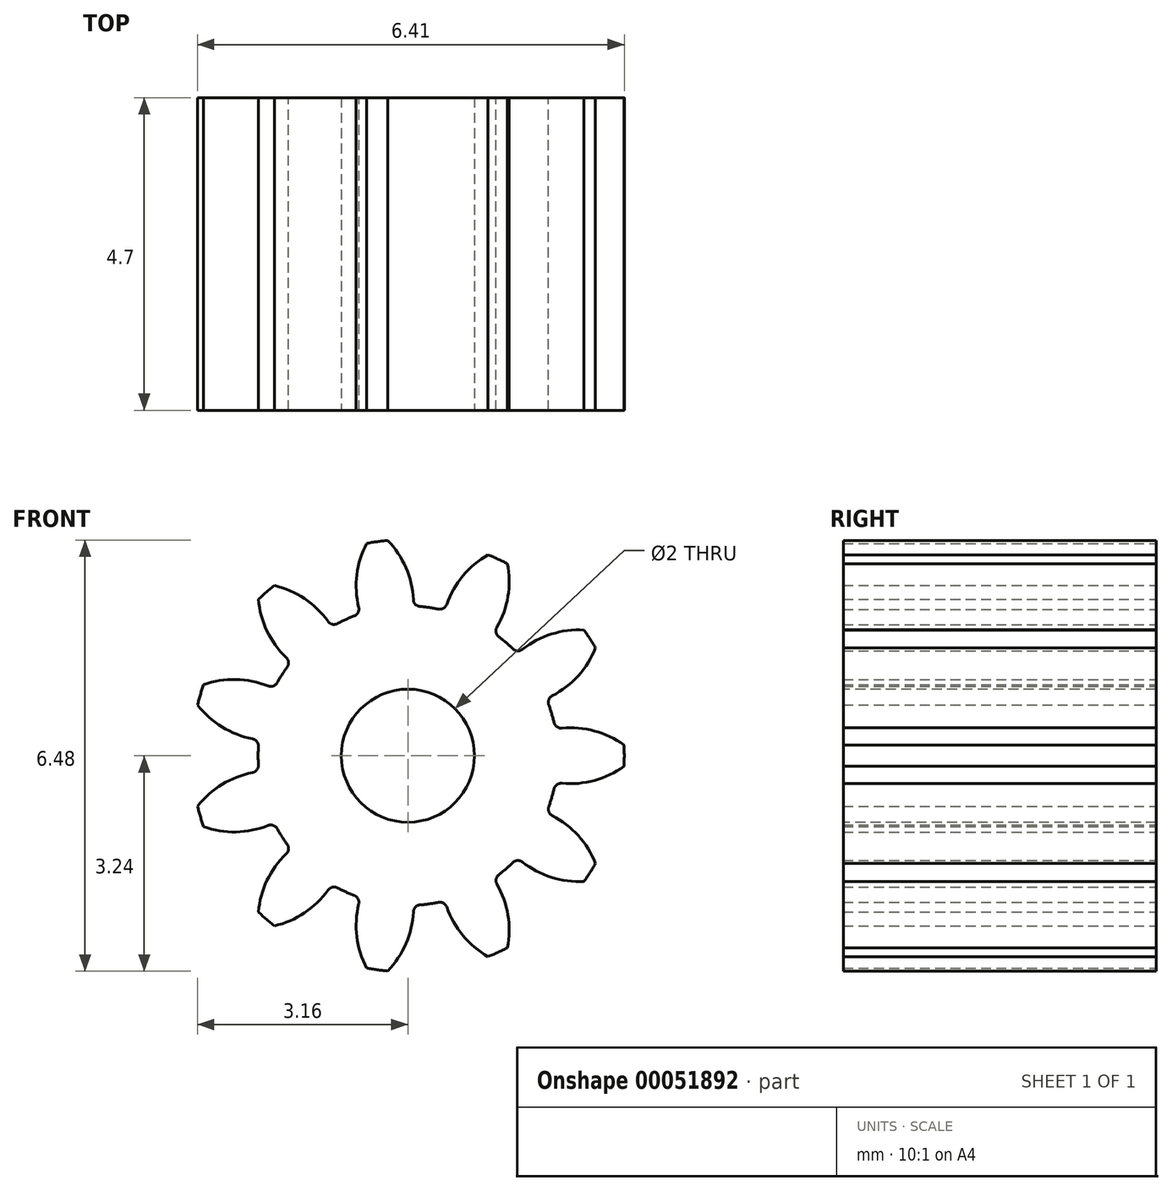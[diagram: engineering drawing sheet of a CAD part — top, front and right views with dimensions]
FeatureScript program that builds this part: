
annotation { "Feature Type Name" : "Feature", "Feature Type Description" : "" }
export const myFeature = defineFeature(function(context is Context, id is Id, definition is map)
    precondition{}
    {
        {
            var Q0;
            Q0=qCreatedBy(makeId("Front.planeOp"),FACE);
            var sketch = newSketch(context, id + "F0", { "sketchPlane" : qUnion([Q0])});
            skCircle(sketch, "E0", {"center": v(0, 0) * mm, "radius": 3.25 * mm, "construction": true});
            skCircle(sketch, "E1", {"center": v(0, 0) * mm, "radius": 2.25 * mm, "construction": true});
            skCircle(sketch, "E2", {"center": v(0, 0) * mm, "radius": 2.75 * mm, "construction": true});
            skLineSegment(sketch, "E3", {"start": v(0, 0) * mm, "end": v(0, 5.25) * mm, "construction": true});
            skLineSegment(sketch, "E4", {"start": v(0, 2.75) * mm, "end": v(-5.58, 2.75) * mm, "construction": true});
            skLineSegment(sketch, "E5", {"start": v(0, 2.75) * mm, "end": v(-4.16, 1.24) * mm, "construction": true});
            skCircle(sketch, "E6", {"center": v(0, 2.75) * mm, "radius": 1.38 * mm, "construction": true});
            skCircle(sketch, "E7.cCircle", {"center": v(0, 0) * mm, "radius": 5.25 * mm, "construction": true});
            skLineSegment(sketch, "E7.0", {"start": v(0, 5.25) * mm, "end": v(0.75, 5.2) * mm, "construction": true});
            skLineSegment(sketch, "E7.1", {"start": v(0.75, 5.2) * mm, "end": v(1.48, 5.04) * mm, "construction": true});
            skLineSegment(sketch, "E7.2", {"start": v(1.48, 5.04) * mm, "end": v(2.18, 4.78) * mm, "construction": true});
            skLineSegment(sketch, "E7.3", {"start": v(2.18, 4.78) * mm, "end": v(2.84, 4.42) * mm, "construction": true});
            skLineSegment(sketch, "E7.4", {"start": v(2.84, 4.42) * mm, "end": v(3.44, 3.97) * mm, "construction": true});
            skLineSegment(sketch, "E7.5", {"start": v(3.44, 3.97) * mm, "end": v(3.97, 3.44) * mm, "construction": true});
            skLineSegment(sketch, "E7.6", {"start": v(3.97, 3.44) * mm, "end": v(4.42, 2.84) * mm, "construction": true});
            skLineSegment(sketch, "E7.7", {"start": v(4.42, 2.84) * mm, "end": v(4.78, 2.18) * mm, "construction": true});
            skLineSegment(sketch, "E7.8", {"start": v(4.78, 2.18) * mm, "end": v(5.04, 1.48) * mm, "construction": true});
            skLineSegment(sketch, "E7.9", {"start": v(5.04, 1.48) * mm, "end": v(5.2, 0.75) * mm, "construction": true});
            skLineSegment(sketch, "E7.10", {"start": v(5.2, 0.75) * mm, "end": v(5.25, 0) * mm, "construction": true});
            skLineSegment(sketch, "E7.11", {"start": v(5.25, 0) * mm, "end": v(5.2, -0.75) * mm, "construction": true});
            skLineSegment(sketch, "E7.12", {"start": v(5.2, -0.75) * mm, "end": v(5.04, -1.48) * mm, "construction": true});
            skLineSegment(sketch, "E7.13", {"start": v(5.04, -1.48) * mm, "end": v(4.78, -2.18) * mm, "construction": true});
            skLineSegment(sketch, "E7.14", {"start": v(4.78, -2.18) * mm, "end": v(4.42, -2.84) * mm, "construction": true});
            skLineSegment(sketch, "E7.15", {"start": v(4.42, -2.84) * mm, "end": v(3.97, -3.44) * mm, "construction": true});
            skLineSegment(sketch, "E7.16", {"start": v(3.97, -3.44) * mm, "end": v(3.44, -3.97) * mm, "construction": true});
            skLineSegment(sketch, "E7.17", {"start": v(3.44, -3.97) * mm, "end": v(2.84, -4.42) * mm, "construction": true});
            skLineSegment(sketch, "E7.18", {"start": v(2.84, -4.42) * mm, "end": v(2.18, -4.78) * mm, "construction": true});
            skLineSegment(sketch, "E7.19", {"start": v(2.18, -4.78) * mm, "end": v(1.48, -5.04) * mm, "construction": true});
            skLineSegment(sketch, "E7.20", {"start": v(1.48, -5.04) * mm, "end": v(0.75, -5.2) * mm, "construction": true});
            skLineSegment(sketch, "E7.21", {"start": v(0.75, -5.2) * mm, "end": v(0, -5.25) * mm, "construction": true});
            skLineSegment(sketch, "E7.22", {"start": v(0, -5.25) * mm, "end": v(-0.75, -5.2) * mm, "construction": true});
            skLineSegment(sketch, "E7.23", {"start": v(-0.75, -5.2) * mm, "end": v(-1.48, -5.04) * mm, "construction": true});
            skLineSegment(sketch, "E7.24", {"start": v(-1.48, -5.04) * mm, "end": v(-2.18, -4.78) * mm, "construction": true});
            skLineSegment(sketch, "E7.25", {"start": v(-2.18, -4.78) * mm, "end": v(-2.84, -4.42) * mm, "construction": true});
            skLineSegment(sketch, "E7.26", {"start": v(-2.84, -4.42) * mm, "end": v(-3.44, -3.97) * mm, "construction": true});
            skLineSegment(sketch, "E7.27", {"start": v(-3.44, -3.97) * mm, "end": v(-3.97, -3.44) * mm, "construction": true});
            skLineSegment(sketch, "E7.28", {"start": v(-3.97, -3.44) * mm, "end": v(-4.42, -2.84) * mm, "construction": true});
            skLineSegment(sketch, "E7.29", {"start": v(-4.42, -2.84) * mm, "end": v(-4.78, -2.18) * mm, "construction": true});
            skLineSegment(sketch, "E7.30", {"start": v(-4.78, -2.18) * mm, "end": v(-5.04, -1.48) * mm, "construction": true});
            skLineSegment(sketch, "E7.31", {"start": v(-5.04, -1.48) * mm, "end": v(-5.2, -0.75) * mm, "construction": true});
            skLineSegment(sketch, "E7.32", {"start": v(-5.2, -0.75) * mm, "end": v(-5.25, 0) * mm, "construction": true});
            skLineSegment(sketch, "E7.33", {"start": v(-5.25, 0) * mm, "end": v(-5.2, 0.75) * mm, "construction": true});
            skLineSegment(sketch, "E7.34", {"start": v(-5.2, 0.75) * mm, "end": v(-5.04, 1.48) * mm, "construction": true});
            skLineSegment(sketch, "E7.35", {"start": v(-5.04, 1.48) * mm, "end": v(-4.78, 2.18) * mm, "construction": true});
            skLineSegment(sketch, "E7.36", {"start": v(-4.78, 2.18) * mm, "end": v(-4.42, 2.84) * mm, "construction": true});
            skLineSegment(sketch, "E7.37", {"start": v(-4.42, 2.84) * mm, "end": v(-3.97, 3.44) * mm, "construction": true});
            skLineSegment(sketch, "E7.38", {"start": v(-3.97, 3.44) * mm, "end": v(-3.44, 3.97) * mm, "construction": true});
            skLineSegment(sketch, "E7.39", {"start": v(-3.44, 3.97) * mm, "end": v(-2.84, 4.42) * mm, "construction": true});
            skLineSegment(sketch, "E7.40", {"start": v(-2.84, 4.42) * mm, "end": v(-2.18, 4.78) * mm, "construction": true});
            skLineSegment(sketch, "E7.41", {"start": v(-2.18, 4.78) * mm, "end": v(-1.48, 5.04) * mm, "construction": true});
            skLineSegment(sketch, "E7.42", {"start": v(-1.48, 5.04) * mm, "end": v(-0.75, 5.2) * mm, "construction": true});
            skLineSegment(sketch, "E7.43", {"start": v(-0.75, 5.2) * mm, "end": v(0, 5.25) * mm, "construction": true});
            skLineSegment(sketch, "E8", {"start": v(-1.48, 5.04) * mm, "end": v(0, 0) * mm, "construction": true});
            skLineSegment(sketch, "E9", {"start": v(-0.75, 5.2) * mm, "end": v(0, 0) * mm, "construction": true});
            skArc(sketch, "E10", {"start": v(0.08, 2.35) * mm, "mid": v(-2.67, 2.26) * mm, "end": v(0.08, 2.25) * mm, "construction": true});
            skArc(sketch, "E11", {"start": v(-0.3, 3.24) * mm, "mid": v(-0.03, 2.83) * mm, "end": v(0.08, 2.35) * mm});
            skArc(sketch, "E12.MirrorCS", {"start": v(-0.62, 3.2) * mm, "mid": v(-0.77, 2.72) * mm, "end": v(-0.74, 2.23) * mm});
            skArc(sketch, "E13", {"start": v(-0.62, 3.2) * mm, "mid": v(-0.46, 3.22) * mm, "end": v(-0.3, 3.24) * mm});
            skArc(sketch, "E14", {"start": v(-0.8, 2.1) * mm, "mid": v(0.32, -2.23) * mm, "end": v(0.18, 2.24) * mm});
            skArc(sketch, "E15.1.0", {"start": v(-2.25, 2.35) * mm, "mid": v(-2.1, 1.83) * mm, "end": v(-1.75, 1.41) * mm});
            skArc(sketch, "E15.1.1", {"start": v(-2.25, 2.35) * mm, "mid": v(-2.13, 2.46) * mm, "end": v(-2, 2.56) * mm});
            skArc(sketch, "E15.1.2", {"start": v(-2, 2.56) * mm, "mid": v(-1.51, 2.33) * mm, "end": v(-1.15, 1.94) * mm});
            skArc(sketch, "E15.2.0", {"start": v(-3.16, 0.76) * mm, "mid": v(-2.75, 0.4) * mm, "end": v(-2.24, 0.24) * mm});
            skArc(sketch, "E15.2.1", {"start": v(-3.16, 0.76) * mm, "mid": v(-3.12, 0.92) * mm, "end": v(-3.07, 1.07) * mm});
            skArc(sketch, "E15.2.2", {"start": v(-3.07, 1.07) * mm, "mid": v(-2.53, 1.14) * mm, "end": v(-2.01, 1) * mm});
            skArc(sketch, "E15.3.0", {"start": v(-3.07, -1.07) * mm, "mid": v(-2.53, -1.14) * mm, "end": v(-2.01, -1) * mm});
            skArc(sketch, "E15.3.1", {"start": v(-3.07, -1.07) * mm, "mid": v(-3.12, -0.92) * mm, "end": v(-3.16, -0.76) * mm});
            skArc(sketch, "E15.3.2", {"start": v(-3.16, -0.76) * mm, "mid": v(-2.75, -0.4) * mm, "end": v(-2.24, -0.24) * mm});
            skArc(sketch, "E15.4.0", {"start": v(-2, -2.56) * mm, "mid": v(-1.51, -2.33) * mm, "end": v(-1.15, -1.94) * mm});
            skArc(sketch, "E15.4.1", {"start": v(-2, -2.56) * mm, "mid": v(-2.13, -2.46) * mm, "end": v(-2.25, -2.35) * mm});
            skArc(sketch, "E15.4.2", {"start": v(-2.25, -2.35) * mm, "mid": v(-2.1, -1.83) * mm, "end": v(-1.75, -1.41) * mm});
            skArc(sketch, "E15.5.0", {"start": v(-0.3, -3.24) * mm, "mid": v(-0.01, -2.78) * mm, "end": v(0.08, -2.25) * mm});
            skArc(sketch, "E15.5.1", {"start": v(-0.3, -3.24) * mm, "mid": v(-0.46, -3.22) * mm, "end": v(-0.62, -3.2) * mm});
            skArc(sketch, "E15.5.2", {"start": v(-0.62, -3.2) * mm, "mid": v(-0.77, -2.67) * mm, "end": v(-0.71, -2.13) * mm});
            skArc(sketch, "E15.6.0", {"start": v(1.5, -2.89) * mm, "mid": v(1.5, -2.35) * mm, "end": v(1.29, -1.85) * mm});
            skArc(sketch, "E15.6.1", {"start": v(1.5, -2.89) * mm, "mid": v(1.35, -2.96) * mm, "end": v(1.2, -3.02) * mm});
            skArc(sketch, "E15.6.2", {"start": v(1.2, -3.02) * mm, "mid": v(0.8, -2.66) * mm, "end": v(0.55, -2.18) * mm});
            skArc(sketch, "E15.7.0", {"start": v(2.82, -1.62) * mm, "mid": v(2.52, -1.17) * mm, "end": v(2.08, -0.86) * mm});
            skArc(sketch, "E15.7.1", {"start": v(2.82, -1.62) * mm, "mid": v(2.73, -1.76) * mm, "end": v(2.64, -1.89) * mm});
            skArc(sketch, "E15.7.2", {"start": v(2.64, -1.89) * mm, "mid": v(2.1, -1.81) * mm, "end": v(1.65, -1.53) * mm});
            skArc(sketch, "E15.8.0", {"start": v(3.25, 0.16) * mm, "mid": v(2.75, 0.38) * mm, "end": v(2.21, 0.4) * mm});
            skArc(sketch, "E15.8.1", {"start": v(3.25, 0.16) * mm, "mid": v(3.25, 0) * mm, "end": v(3.25, -0.16) * mm});
            skArc(sketch, "E15.8.2", {"start": v(3.25, -0.16) * mm, "mid": v(2.75, -0.38) * mm, "end": v(2.21, -0.4) * mm});
            skArc(sketch, "E15.9.0", {"start": v(2.64, 1.89) * mm, "mid": v(2.1, 1.81) * mm, "end": v(1.65, 1.53) * mm});
            skArc(sketch, "E15.9.1", {"start": v(2.64, 1.89) * mm, "mid": v(2.73, 1.76) * mm, "end": v(2.82, 1.62) * mm});
            skArc(sketch, "E15.9.2", {"start": v(2.82, 1.62) * mm, "mid": v(2.52, 1.17) * mm, "end": v(2.08, 0.86) * mm});
            skArc(sketch, "E15.10.0", {"start": v(1.2, 3.02) * mm, "mid": v(0.8, 2.66) * mm, "end": v(0.55, 2.18) * mm});
            skArc(sketch, "E15.10.1", {"start": v(1.2, 3.02) * mm, "mid": v(1.35, 2.96) * mm, "end": v(1.5, 2.89) * mm});
            skArc(sketch, "E15.10.2", {"start": v(1.5, 2.89) * mm, "mid": v(1.5, 2.35) * mm, "end": v(1.29, 1.85) * mm});
            skPoint(sketch, "E16.visualSharp", {"position": v(0.08, 2.25) * mm});
            skArc(sketch, "E16.filletArc", {"start": v(0.08, 2.35) * mm, "mid": v(0.11, 2.28) * mm, "end": v(0.18, 2.24) * mm});
            skPoint(sketch, "E17.visualSharp", {"position": v(-0.71, 2.13) * mm});
            skArc(sketch, "E17.filletArc", {"start": v(-0.8, 2.1) * mm, "mid": v(-0.75, 2.15) * mm, "end": v(-0.74, 2.23) * mm});
            skArc(sketch, "E18.1.0", {"start": v(-2, 2.56) * mm, "mid": v(-1.55, 2.36) * mm, "end": v(-1.2, 2.02) * mm});
            skArc(sketch, "E18.1.2", {"start": v(-2.25, 2.35) * mm, "mid": v(-2.12, 1.87) * mm, "end": v(-1.83, 1.48) * mm});
            skArc(sketch, "E18.1.3", {"start": v(-1.81, 1.33) * mm, "mid": v(-1.8, 1.4) * mm, "end": v(-1.83, 1.48) * mm});
            skArc(sketch, "E18.1.4", {"start": v(-1.2, 2.02) * mm, "mid": v(-1.14, 1.98) * mm, "end": v(-1.06, 1.99) * mm});
            skArc(sketch, "E18.2.0", {"start": v(-3.07, 1.07) * mm, "mid": v(-2.58, 1.15) * mm, "end": v(-2.1, 1.05) * mm});
            skArc(sketch, "E18.2.2", {"start": v(-3.16, 0.76) * mm, "mid": v(-2.8, 0.43) * mm, "end": v(-2.33, 0.25) * mm});
            skArc(sketch, "E18.2.3", {"start": v(-2.25, 0.14) * mm, "mid": v(-2.27, 0.21) * mm, "end": v(-2.33, 0.25) * mm});
            skArc(sketch, "E18.2.4", {"start": v(-2.1, 1.05) * mm, "mid": v(-2.02, 1.05) * mm, "end": v(-1.96, 1.1) * mm});
            skArc(sketch, "E18.3.0", {"start": v(-3.16, -0.76) * mm, "mid": v(-2.8, -0.43) * mm, "end": v(-2.33, -0.25) * mm});
            skArc(sketch, "E18.3.2", {"start": v(-3.07, -1.07) * mm, "mid": v(-2.58, -1.15) * mm, "end": v(-2.1, -1.05) * mm});
            skArc(sketch, "E18.3.3", {"start": v(-1.96, -1.1) * mm, "mid": v(-2.02, -1.05) * mm, "end": v(-2.1, -1.05) * mm});
            skArc(sketch, "E18.3.4", {"start": v(-2.33, -0.25) * mm, "mid": v(-2.27, -0.21) * mm, "end": v(-2.25, -0.14) * mm});
            skArc(sketch, "E18.4.0", {"start": v(-2.25, -2.35) * mm, "mid": v(-2.12, -1.87) * mm, "end": v(-1.83, -1.48) * mm});
            skArc(sketch, "E18.4.2", {"start": v(-2, -2.56) * mm, "mid": v(-1.55, -2.36) * mm, "end": v(-1.2, -2.02) * mm});
            skArc(sketch, "E18.4.3", {"start": v(-1.06, -1.99) * mm, "mid": v(-1.14, -1.98) * mm, "end": v(-1.2, -2.02) * mm});
            skArc(sketch, "E18.4.4", {"start": v(-1.83, -1.48) * mm, "mid": v(-1.8, -1.4) * mm, "end": v(-1.81, -1.33) * mm});
            skArc(sketch, "E18.5.0", {"start": v(-0.62, -3.2) * mm, "mid": v(-0.77, -2.72) * mm, "end": v(-0.74, -2.23) * mm});
            skArc(sketch, "E18.5.2", {"start": v(-0.3, -3.24) * mm, "mid": v(-0.03, -2.83) * mm, "end": v(0.08, -2.35) * mm});
            skArc(sketch, "E18.5.3", {"start": v(0.18, -2.24) * mm, "mid": v(0.11, -2.28) * mm, "end": v(0.08, -2.35) * mm});
            skArc(sketch, "E18.5.4", {"start": v(-0.74, -2.23) * mm, "mid": v(-0.75, -2.15) * mm, "end": v(-0.8, -2.1) * mm});
            skArc(sketch, "E18.6.0", {"start": v(1.2, -3.02) * mm, "mid": v(0.83, -2.7) * mm, "end": v(0.58, -2.27) * mm});
            skArc(sketch, "E18.6.2", {"start": v(1.5, -2.89) * mm, "mid": v(1.5, -2.4) * mm, "end": v(1.34, -1.93) * mm});
            skArc(sketch, "E18.6.3", {"start": v(1.37, -1.79) * mm, "mid": v(1.32, -1.85) * mm, "end": v(1.34, -1.93) * mm});
            skArc(sketch, "E18.6.4", {"start": v(0.58, -2.27) * mm, "mid": v(0.53, -2.22) * mm, "end": v(0.46, -2.2) * mm});
            skArc(sketch, "E18.7.0", {"start": v(2.64, -1.89) * mm, "mid": v(2.16, -1.83) * mm, "end": v(1.72, -1.6) * mm});
            skArc(sketch, "E18.7.2", {"start": v(2.82, -1.62) * mm, "mid": v(2.56, -1.2) * mm, "end": v(2.17, -0.9) * mm});
            skArc(sketch, "E18.7.3", {"start": v(2.12, -0.77) * mm, "mid": v(2.12, -0.84) * mm, "end": v(2.17, -0.9) * mm});
            skArc(sketch, "E18.7.4", {"start": v(1.72, -1.6) * mm, "mid": v(1.65, -1.58) * mm, "end": v(1.58, -1.6) * mm});
            skArc(sketch, "E18.8.0", {"start": v(3.25, -0.16) * mm, "mid": v(2.8, -0.37) * mm, "end": v(2.31, -0.41) * mm});
            skArc(sketch, "E18.8.2", {"start": v(3.25, 0.16) * mm, "mid": v(2.8, 0.37) * mm, "end": v(2.31, 0.41) * mm});
            skArc(sketch, "E18.8.3", {"start": v(2.2, 0.5) * mm, "mid": v(2.24, 0.43) * mm, "end": v(2.31, 0.41) * mm});
            skArc(sketch, "E18.8.4", {"start": v(2.31, -0.41) * mm, "mid": v(2.24, -0.43) * mm, "end": v(2.2, -0.5) * mm});
            skArc(sketch, "E18.9.0", {"start": v(2.82, 1.62) * mm, "mid": v(2.56, 1.2) * mm, "end": v(2.17, 0.9) * mm});
            skArc(sketch, "E18.9.2", {"start": v(2.64, 1.89) * mm, "mid": v(2.16, 1.83) * mm, "end": v(1.72, 1.6) * mm});
            skArc(sketch, "E18.9.3", {"start": v(1.58, 1.6) * mm, "mid": v(1.65, 1.58) * mm, "end": v(1.72, 1.6) * mm});
            skArc(sketch, "E18.9.4", {"start": v(2.17, 0.9) * mm, "mid": v(2.12, 0.84) * mm, "end": v(2.12, 0.77) * mm});
            skArc(sketch, "E18.10.0", {"start": v(1.5, 2.89) * mm, "mid": v(1.5, 2.4) * mm, "end": v(1.34, 1.93) * mm});
            skArc(sketch, "E18.10.2", {"start": v(1.2, 3.02) * mm, "mid": v(0.83, 2.7) * mm, "end": v(0.58, 2.27) * mm});
            skArc(sketch, "E18.10.3", {"start": v(0.46, 2.2) * mm, "mid": v(0.53, 2.22) * mm, "end": v(0.58, 2.27) * mm});
            skArc(sketch, "E18.10.4", {"start": v(1.34, 1.93) * mm, "mid": v(1.32, 1.85) * mm, "end": v(1.37, 1.79) * mm});
            skSolve(sketch);
        }
        {
            var Q0;
            Q0 = qSketchRegion(id + "F0", true);
            extrude(context, id + "F1", {"entities" : qUnion([Q0]), "depth" : 4.7 * mm});
        }
        {
            var Q0;
            Q0=makeQuery(id+"F1.opExtrude","CAP_FACE",FACE,{"disambiguationData":[OSD([sQuery(id+"F0.wireOp",EDGE,"E11"),sQuery(id+"F0.wireOp",EDGE,"E12.MirrorCS"),sQuery(id+"F0.wireOp",EDGE,"E13"),sQuery(id+"F0.wireOp",EDGE,"E14"),sQuery(id+"F0.wireOp",EDGE,"E15.1.0"),sQuery(id+"F0.wireOp",EDGE,"E15.1.1"),sQuery(id+"F0.wireOp",EDGE,"E15.1.2"),sQuery(id+"F0.wireOp",EDGE,"E15.2.0"),sQuery(id+"F0.wireOp",EDGE,"E15.2.1"),sQuery(id+"F0.wireOp",EDGE,"E15.2.2"),sQuery(id+"F0.wireOp",EDGE,"E15.3.0"),sQuery(id+"F0.wireOp",EDGE,"E15.3.1"),sQuery(id+"F0.wireOp",EDGE,"E15.3.2"),sQuery(id+"F0.wireOp",EDGE,"E15.4.0"),sQuery(id+"F0.wireOp",EDGE,"E15.4.1"),sQuery(id+"F0.wireOp",EDGE,"E15.4.2"),sQuery(id+"F0.wireOp",EDGE,"E15.5.0"),sQuery(id+"F0.wireOp",EDGE,"E15.5.1"),sQuery(id+"F0.wireOp",EDGE,"E15.5.2"),sQuery(id+"F0.wireOp",EDGE,"E15.6.0"),sQuery(id+"F0.wireOp",EDGE,"E15.6.1"),sQuery(id+"F0.wireOp",EDGE,"E15.6.2"),sQuery(id+"F0.wireOp",EDGE,"E15.7.0"),sQuery(id+"F0.wireOp",EDGE,"E15.7.1"),sQuery(id+"F0.wireOp",EDGE,"E15.7.2"),sQuery(id+"F0.wireOp",EDGE,"E15.8.0"),sQuery(id+"F0.wireOp",EDGE,"E15.8.1"),sQuery(id+"F0.wireOp",EDGE,"E15.8.2"),sQuery(id+"F0.wireOp",EDGE,"E15.9.0"),sQuery(id+"F0.wireOp",EDGE,"E15.9.1"),sQuery(id+"F0.wireOp",EDGE,"E15.9.2"),sQuery(id+"F0.wireOp",EDGE,"E15.10.0"),sQuery(id+"F0.wireOp",EDGE,"E15.10.1"),sQuery(id+"F0.wireOp",EDGE,"E15.10.2")])],"isStart":false});
            var sketch = newSketch(context, id + "F2", { "sketchPlane" : qUnion([Q0])});
            skCircle(sketch, "E19", {"center": v(0, 0) * mm, "radius": 1 * mm});
            skSolve(sketch);
        }
        {
            var Q0;
            Q0 = qSketchRegion(id + "F2", true);
            extrude(context, id + "F3", {"entities" : qUnion([Q0]), "operationType" : NewBodyOperationType.REMOVE, "endBound" : BoundingType.THROUGH_ALL, "oppositeDirection" : true, "depth" : 25 * mm});
        }
    });
